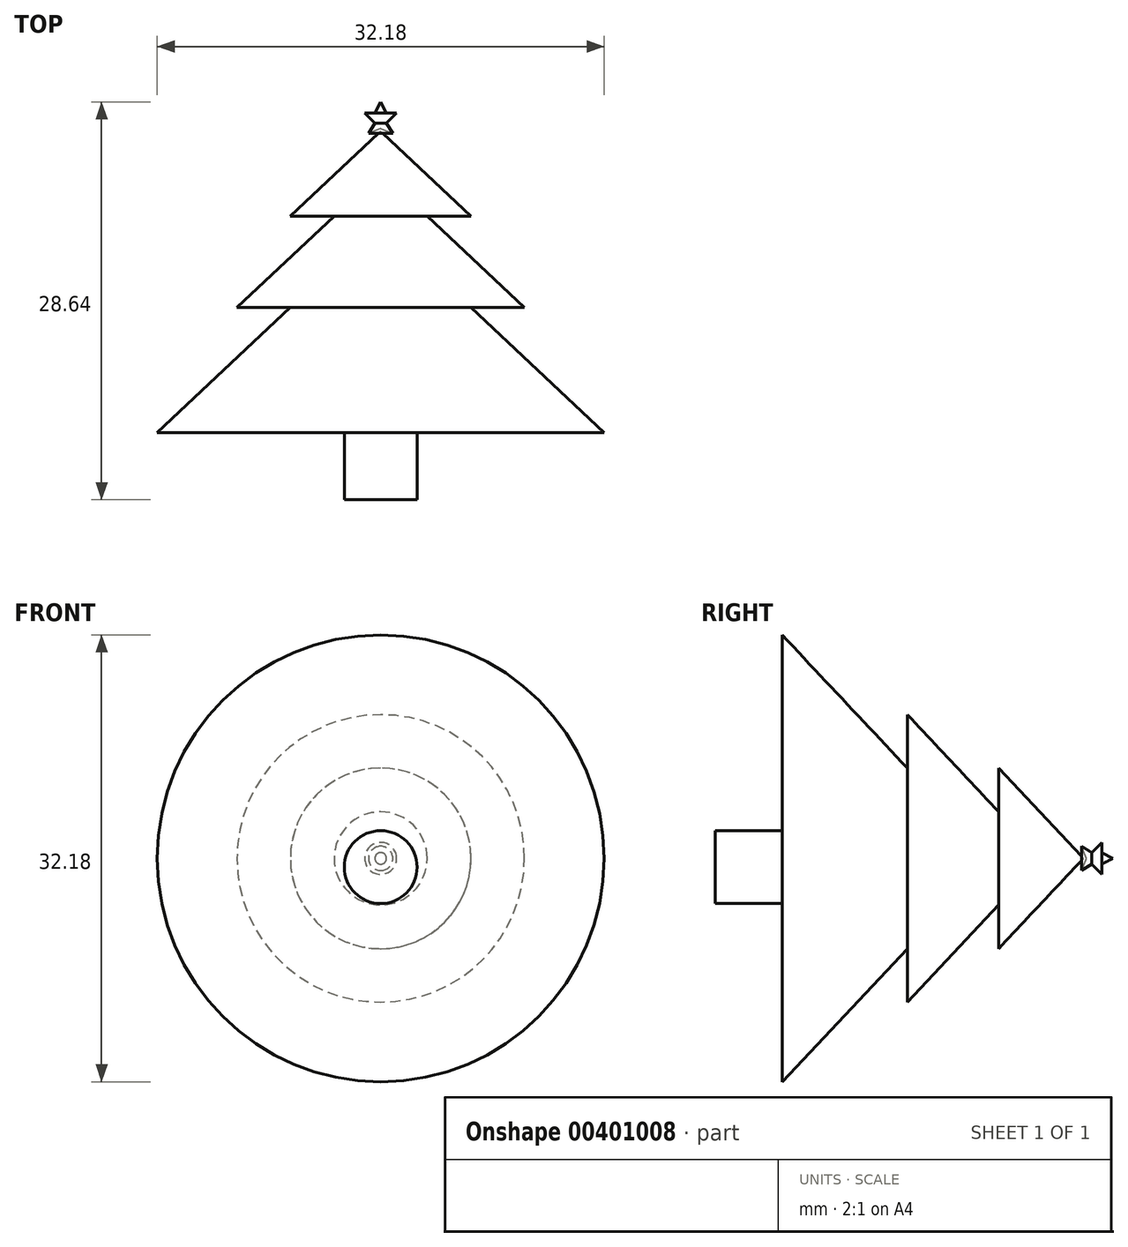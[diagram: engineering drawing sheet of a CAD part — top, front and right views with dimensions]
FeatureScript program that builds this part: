
annotation { "Feature Type Name" : "Feature", "Feature Type Description" : "" }
export const myFeature = defineFeature(function(context is Context, id is Id, definition is map)
    precondition{}
    {
        {
            var Q0;
            Q0=qCreatedBy(makeId("Top.planeOp"),FACE);
            var sketch = newSketch(context, id + "F0", { "sketchPlane" : qUnion([Q0])});
            skLineSegment(sketch, "E0", {"start": v(0, 37.84) * mm, "end": v(-6.5, 31.73) * mm});
            skLineSegment(sketch, "E1", {"start": v(0, 37.84) * mm, "end": v(5.74, 31.73) * mm});
            skLineSegment(sketch, "E2", {"start": v(5.74, 31.73) * mm, "end": v(2.96, 31.73) * mm});
            skLineSegment(sketch, "E3", {"start": v(-6.5, 31.73) * mm, "end": v(-3.35, 31.73) * mm});
            skLineSegment(sketch, "E4", {"start": v(-3.35, 31.73) * mm, "end": v(-10.35, 25.15) * mm});
            skLineSegment(sketch, "E5", {"start": v(-10.35, 25.15) * mm, "end": v(-6.5, 25.15) * mm});
            skLineSegment(sketch, "E6", {"start": v(2.96, 31.73) * mm, "end": v(9.13, 25.15) * mm});
            skLineSegment(sketch, "E7", {"start": v(9.13, 25.15) * mm, "end": v(5.74, 25.15) * mm});
            skLineSegment(sketch, "E8", {"start": v(-6.5, 25.15) * mm, "end": v(-16.1, 16.14) * mm});
            skLineSegment(sketch, "E9", {"start": v(5.74, 25.15) * mm, "end": v(14.2, 16.14) * mm});
            skLineSegment(sketch, "E10", {"start": v(14.2, 16.14) * mm, "end": v(-16.1, 16.14) * mm});
            skLineSegment(sketch, "E11", {"start": v(0, 37.84) * mm, "end": v(0, 16.14) * mm});
            skSolve(sketch);
        }
        {
            var Q0;
            Q0=makeQuery(id+"F0.imprint","IMPRINT",FACE,{"disambiguationData":[TD([[makeQuery(id+"F0.imprint","IMPRINT",EDGE,{"derivedFrom":sQuery(id+"F0.wireOp",EDGE,"E0")}),1.0]])]});
            var Q1;
            Q1=sQuery(id+"F0.wireOp",EDGE,"E11");
            revolve(context, id + "F1", {"entities" : qUnion([Q0]), "axis" : qUnion([Q1]), "revolveType" : RevolveType.FULL});
        }
        {
            var Q0;
            Q0=makeQuery(id+"F1.opRevolve","SWEPT_FACE",FACE,{"disambiguationData":[OSD([sQuery(id+"F0.wireOp",EDGE,"E10")])]});
            var sketch = newSketch(context, id + "F2", { "sketchPlane" : qUnion([Q0])});
            skCircle(sketch, "E12", {"center": v(0, -0.63) * mm, "radius": 2.63 * mm});
            skSolve(sketch);
        }
        {
            var Q0;
            Q0=makeQuery(id+"F2.imprint","IMPRINT",FACE,{"disambiguationData":[TD([[makeQuery(id+"F2.imprint","IMPRINT",EDGE,{"derivedFrom":sQuery(id+"F2.wireOp",EDGE,"E12")}),1.0]])]});
            extrude(context, id + "F3", {"entities" : qUnion([Q0]), "operationType" : NewBodyOperationType.ADD, "depth" : 4.83 * mm});
        }
        {
            var Q0;
            Q0=qCreatedBy(makeId("Top.planeOp"),FACE);
            var sketch = newSketch(context, id + "F4", { "sketchPlane" : qUnion([Q0])});
            skLineSegment(sketch, "E13", {"start": v(0, 39.96) * mm, "end": v(-0.42, 39.16) * mm});
            skLineSegment(sketch, "E14", {"start": v(-0.42, 39.16) * mm, "end": v(-1.15, 39.16) * mm});
            skLineSegment(sketch, "E15", {"start": v(0, 39.96) * mm, "end": v(0.6, 39.16) * mm});
            skPoint(sketch, "E15.endSnap0", {"position": v(-0.78, 39.16) * mm});
            skLineSegment(sketch, "E16", {"start": v(0.6, 39.16) * mm, "end": v(1.29, 39.16) * mm});
            skLineSegment(sketch, "E17", {"start": v(1.29, 39.16) * mm, "end": v(0.6, 38.43) * mm});
            skLineSegment(sketch, "E18", {"start": v(0.6, 38.43) * mm, "end": v(1.29, 37.76) * mm});
            skLineSegment(sketch, "E19", {"start": v(1.29, 37.76) * mm, "end": v(0, 38.04) * mm});
            skLineSegment(sketch, "E20", {"start": v(0, 38.04) * mm, "end": v(-0.87, 37.7) * mm});
            skLineSegment(sketch, "E21", {"start": v(-0.87, 37.7) * mm, "end": v(-0.42, 38.43) * mm});
            skLineSegment(sketch, "E22", {"start": v(-0.42, 38.43) * mm, "end": v(-1.15, 39.16) * mm});
            skLineSegment(sketch, "E23", {"start": v(0, 39.96) * mm, "end": v(0, 38.04) * mm});
            skSolve(sketch);
        }
        {
            var Q0;
            Q0=makeQuery(id+"F4.imprint","IMPRINT",FACE,{"disambiguationData":[TD([[makeQuery(id+"F4.imprint","IMPRINT",EDGE,{"derivedFrom":sQuery(id+"F4.wireOp",EDGE,"E13")}),1.0]])]});
            var Q1;
            Q1=sQuery(id+"F4.wireOp",EDGE,"E23");
            revolve(context, id + "F5", {"entities" : qUnion([Q0]), "axis" : qUnion([Q1]), "revolveType" : RevolveType.FULL});
        }
    });
